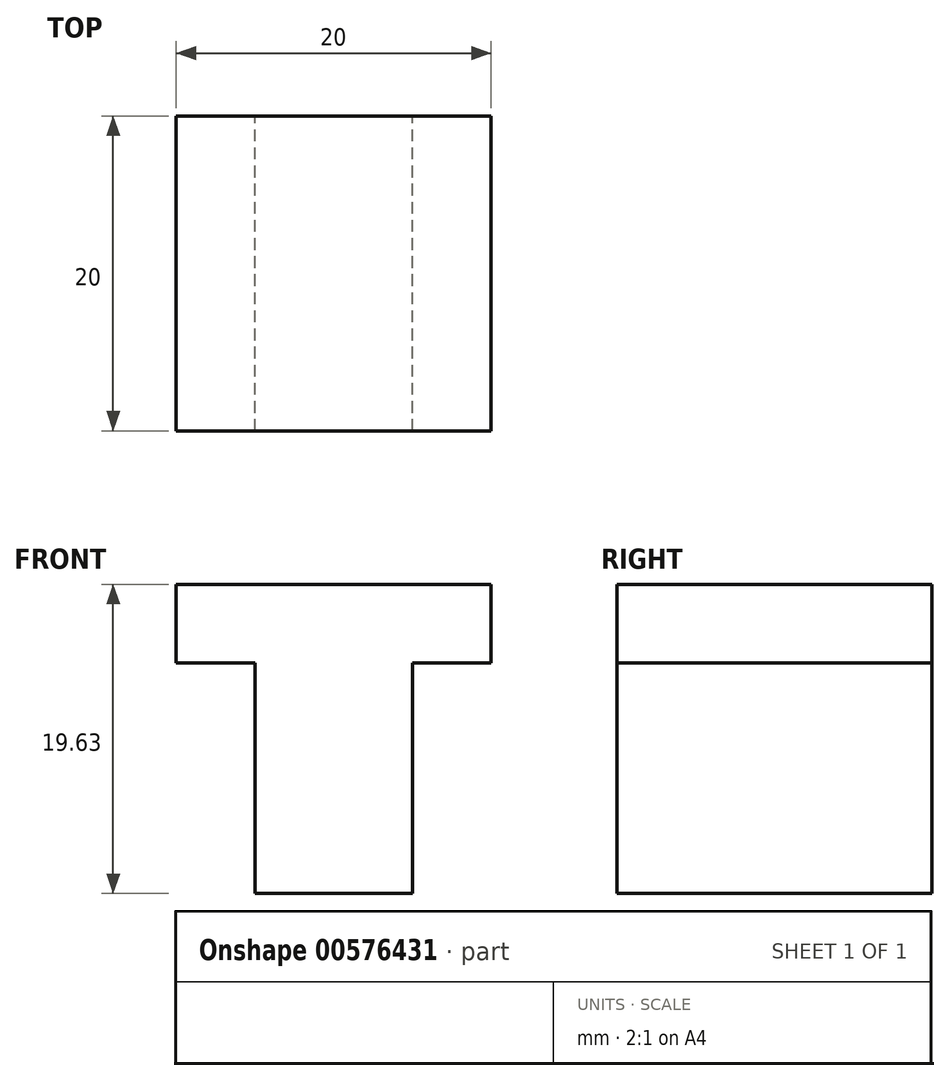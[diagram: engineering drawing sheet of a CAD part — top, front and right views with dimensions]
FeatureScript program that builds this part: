
annotation { "Feature Type Name" : "Feature", "Feature Type Description" : "" }
export const myFeature = defineFeature(function(context is Context, id is Id, definition is map)
    precondition{}
    {
        {
            var Q0;
            Q0=qCreatedBy(makeId("Front.planeOp"),FACE);
            var sketch = newSketch(context, id + "F0", { "sketchPlane" : qUnion([Q0])});
            skLineSegment(sketch, "E0", {"start": v(-41.35, 9.4) * mm, "end": v(-21.35, 9.4) * mm});
            skLineSegment(sketch, "E1", {"start": v(-21.35, 9.4) * mm, "end": v(-21.35, 4.4) * mm});
            skLineSegment(sketch, "E2", {"start": v(-21.35, 4.4) * mm, "end": v(-26.35, 4.4) * mm});
            skLineSegment(sketch, "E3", {"start": v(-26.35, 4.4) * mm, "end": v(-26.35, -10.6) * mm});
            skLineSegment(sketch, "E4", {"start": v(-26.35, -10.22) * mm, "end": v(-36.35, -10.22) * mm});
            skLineSegment(sketch, "E5", {"start": v(-36.35, -10.22) * mm, "end": v(-36.35, 4.4) * mm});
            skLineSegment(sketch, "E6", {"start": v(-36.35, 4.4) * mm, "end": v(-41.35, 4.4) * mm});
            skLineSegment(sketch, "E7", {"start": v(-41.35, 4.4) * mm, "end": v(-41.35, 9.4) * mm});
            skSolve(sketch);
        }
        {
            var Q0;
            Q0=makeQuery(id+"F0.imprint","IMPRINT",FACE,{"disambiguationData":[TD([[makeQuery(id+"F0.imprint","IMPRINT",EDGE,{"derivedFrom":sQuery(id+"F0.wireOp",EDGE,"E0")}),-1.0]])]});
            extrude(context, id + "F1", {"entities" : qUnion([Q0]), "depth" : 20 * mm, "offsetDistance" : 25 * mm});
        }
    });
